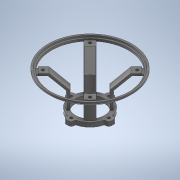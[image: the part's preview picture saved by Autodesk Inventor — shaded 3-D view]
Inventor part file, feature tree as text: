
AUTODESK INVENTOR PART (.ipt)
format: ipt  version: 2020 (Build 240168000, 168)  size: 466,432 bytes
history: native  units: mm
features: other x11, sketch x8, revolve x4, extrude x3, projected_geometry x3, pattern_circular x1, fillet x1
ambient origin geometry x8: Origin, YZ Plane, XZ Plane, XY Plane, X Axis, Y Axis, Z Axis, Center Point
bodies: Body1 (feature_tree)
feature tree (31):
  other  "Твердое тело1"
  extrude  "Выдавливание1"  Depth=34.0mm
  other  "РабПлоскость1"
  other  "РабОсь1"
  revolve  "Вращение1"
  sketch  "Эскиз3"
  other  "РабТочка1"
  extrude  "Выдавливание2"  Depth=45.0mm
  other  "РабТочка2"
  other  "РабТочка3"
  other  "РабТочка4"
  other  "РабПлоскость2"
  sketch  "Эскиз5"
  revolve  "Вращение2"
  revolve  "Вращение3"
  pattern_circular  "Круговой массив1"  Angle=45.0deg  [1 undecoded]
  extrude  "Выдавливание3"  Depth=3.3mm
  revolve  "Вращение4"
  sketch  "Эскиз8"
  fillet  "Сопряжение1"  Radius=9.0mm
  sketch  "Эскиз1"
  sketch  "Эскиз2"
  sketch  "Эскиз4"
  projected_geometry  "Спроецированная петля1"
  projected_geometry  "Спроецированная петля2"
  projected_geometry  "Спроецированная петля3"
  other  "РабПлоскость3"
  other  "РабПлоскость4"
  other  "РабПлоскость5"
  sketch  "Эскиз6"
  sketch  "Эскиз7"
note: 1 required parameter value undecoded (feature->parameter linkage not recoverable at this tier; creation-order binding heuristic only, values carry confidence <= 0.55)
